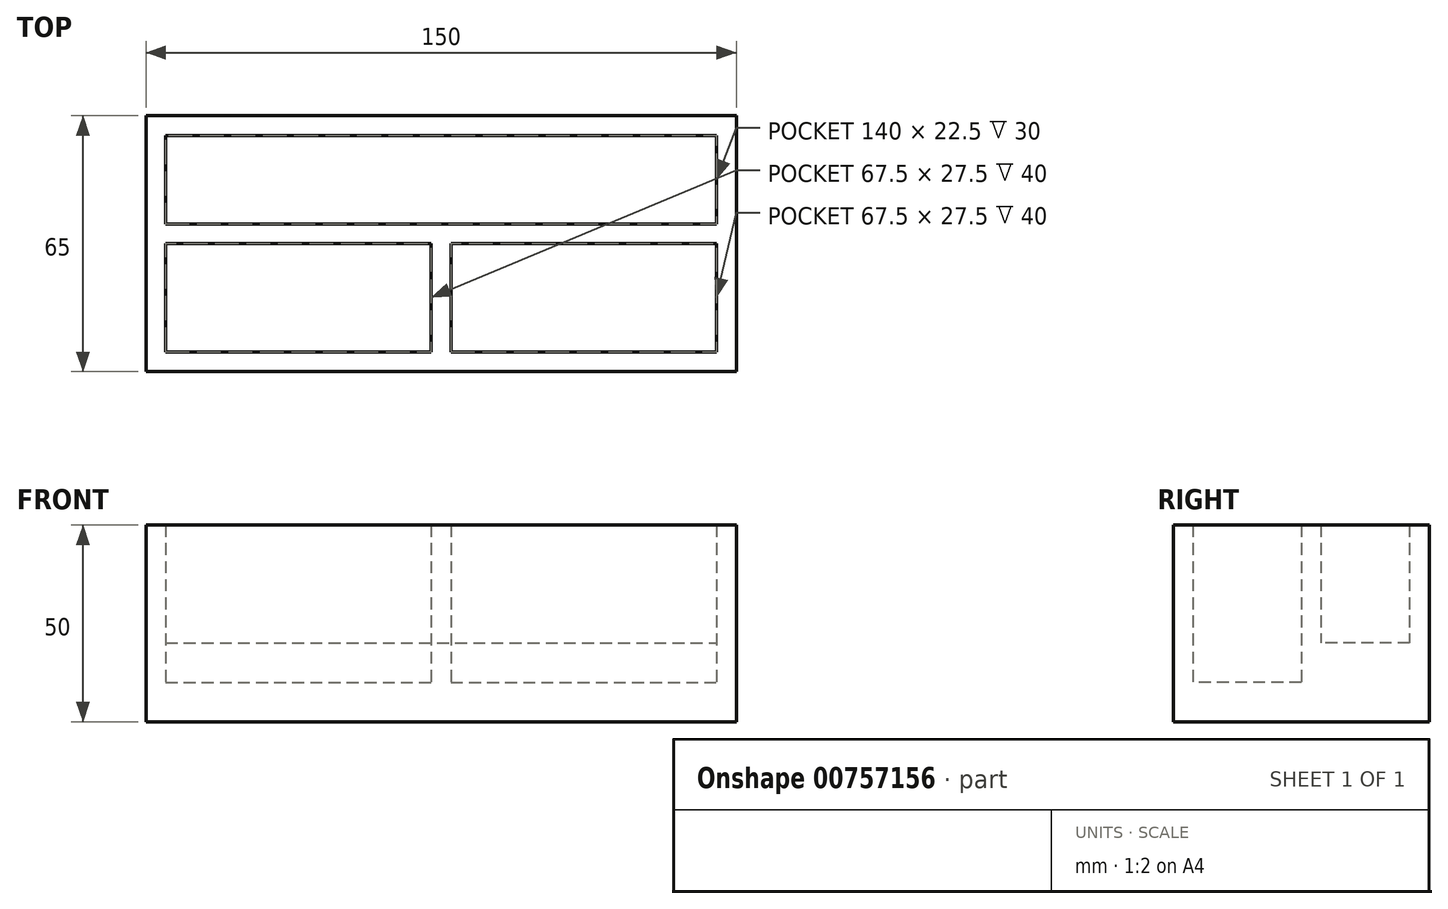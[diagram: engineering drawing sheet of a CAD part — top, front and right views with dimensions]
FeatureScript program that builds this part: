
annotation { "Feature Type Name" : "Feature", "Feature Type Description" : "" }
export const myFeature = defineFeature(function(context is Context, id is Id, definition is map)
    precondition{}
    {
        {
            var Q0;
            Q0=qCreatedBy(makeId("Top.planeOp"),FACE);
            var sketch = newSketch(context, id + "F0", { "sketchPlane" : qUnion([Q0])});
            skLineSegment(sketch, "E0.bottom", {"start": v(-75, 30) * mm, "end": v(75, 30) * mm});
            skLineSegment(sketch, "E0.top", {"start": v(-75, -35) * mm, "end": v(75, -35) * mm});
            skLineSegment(sketch, "E0.left", {"start": v(-75, 30) * mm, "end": v(-75, -35) * mm});
            skLineSegment(sketch, "E0.right", {"start": v(75, 30) * mm, "end": v(75, -35) * mm});
            skLineSegment(sketch, "E1.bottom", {"start": v(-70, 25) * mm, "end": v(70, 25) * mm});
            skLineSegment(sketch, "E1.left", {"start": v(-70, 25) * mm, "end": v(-70, 2.5) * mm});
            skLineSegment(sketch, "E1.right", {"start": v(70, 25) * mm, "end": v(70, 2.5) * mm});
            skLineSegment(sketch, "E2", {"start": v(-70, 2.5) * mm, "end": v(70, 2.5) * mm});
            skLineSegment(sketch, "E3.bottom", {"start": v(-70, -2.5) * mm, "end": v(-2.5, -2.5) * mm});
            skLineSegment(sketch, "E3.top", {"start": v(-70, -30) * mm, "end": v(-2.5, -30) * mm});
            skLineSegment(sketch, "E3.left", {"start": v(-70, -2.5) * mm, "end": v(-70, -30) * mm});
            skLineSegment(sketch, "E3.right", {"start": v(-2.5, -2.5) * mm, "end": v(-2.5, -30) * mm});
            skLineSegment(sketch, "E4.bottom", {"start": v(2.5, -2.5) * mm, "end": v(70, -2.5) * mm});
            skLineSegment(sketch, "E4.top", {"start": v(2.5, -30) * mm, "end": v(70, -30) * mm});
            skLineSegment(sketch, "E4.left", {"start": v(2.5, -2.5) * mm, "end": v(2.5, -30) * mm});
            skLineSegment(sketch, "E4.right", {"start": v(70, -2.5) * mm, "end": v(70, -30) * mm});
            skSolve(sketch);
        }
        {
            var Q0;
            Q0=makeQuery(id+"F0.imprint","IMPRINT",FACE,{"disambiguationData":[TD([[makeQuery(id+"F0.imprint","IMPRINT",EDGE,{"derivedFrom":sQuery(id+"F0.wireOp",EDGE,"E0.bottom")}),-1.0]])]});
            extrude(context, id + "F1", {"entities" : qUnion([Q0]), "depth" : 50 * mm, "offsetDistance" : 25 * mm});
        }
        {
            var Q0;
            Q0=makeQuery(id+"F0.imprint","IMPRINT",FACE,{"disambiguationData":[TD([[makeQuery(id+"F0.imprint","IMPRINT",EDGE,{"derivedFrom":sQuery(id+"F0.wireOp",EDGE,"E1.bottom")}),-1.0]])]});
            extrude(context, id + "F2", {"entities" : qUnion([Q0]), "operationType" : NewBodyOperationType.ADD, "depth" : 20 * mm, "offsetDistance" : 25 * mm});
        }
        {
            var Q0;
            Q0=makeQuery(id+"F0.imprint","IMPRINT",FACE,{"disambiguationData":[TD([[makeQuery(id+"F0.imprint","IMPRINT",EDGE,{"derivedFrom":sQuery(id+"F0.wireOp",EDGE,"E3.bottom")}),-1.0]])]});
            var Q1;
            Q1=makeQuery(id+"F0.imprint","IMPRINT",FACE,{"disambiguationData":[TD([[makeQuery(id+"F0.imprint","IMPRINT",EDGE,{"derivedFrom":sQuery(id+"F0.wireOp",EDGE,"E4.bottom")}),-1.0]])]});
            extrude(context, id + "F3", {"entities" : qUnion([Q0, Q1]), "operationType" : NewBodyOperationType.ADD, "depth" : 10 * mm, "offsetDistance" : 25 * mm});
        }
    });
